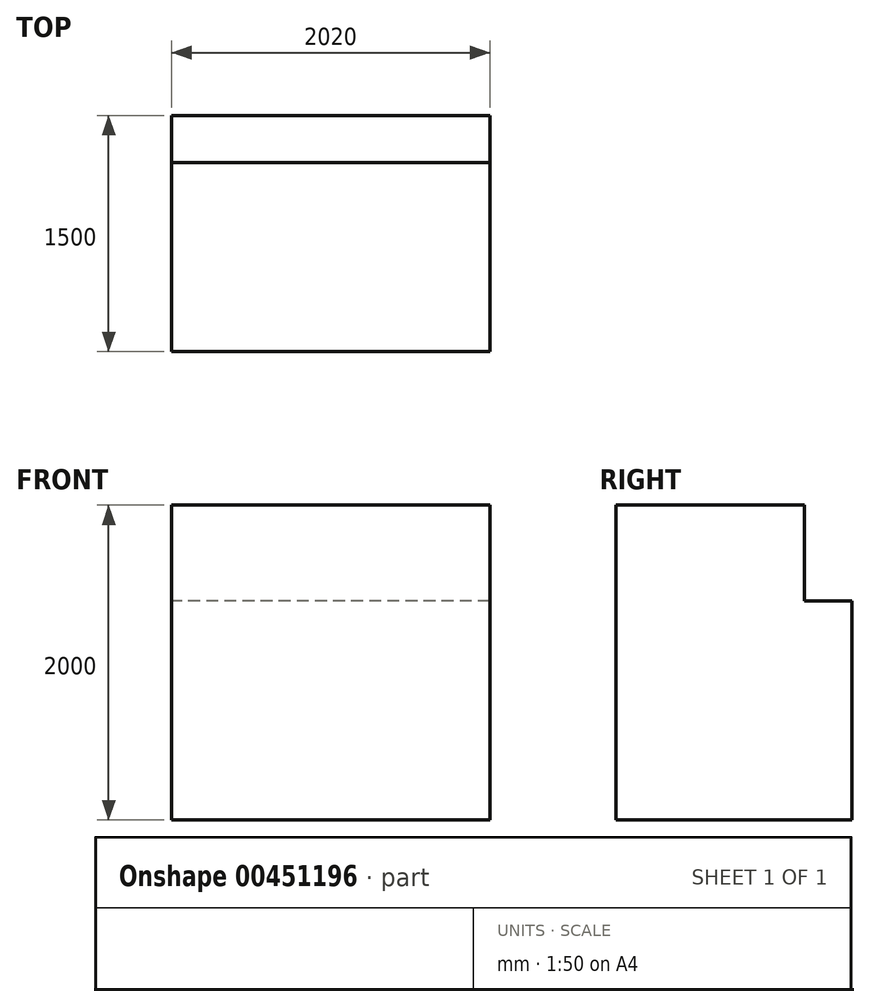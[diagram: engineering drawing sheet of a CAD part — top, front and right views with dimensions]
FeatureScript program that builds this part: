
annotation { "Feature Type Name" : "Feature", "Feature Type Description" : "" }
export const myFeature = defineFeature(function(context is Context, id is Id, definition is map)
    precondition{}
    {
        {
            var Q0;
            Q0=qCreatedBy(makeId("Top.planeOp"),FACE);
            var sketch = newSketch(context, id + "F0", { "sketchPlane" : qUnion([Q0])});
            skLineSegment(sketch, "E0.bottom", {"start": v(1010, -750) * mm, "end": v(-1010, -750) * mm});
            skLineSegment(sketch, "E0.top", {"start": v(1010, 750) * mm, "end": v(-1010, 750) * mm});
            skLineSegment(sketch, "E0.left", {"start": v(1010, -750) * mm, "end": v(1010, 750) * mm});
            skLineSegment(sketch, "E0.right", {"start": v(-1010, -750) * mm, "end": v(-1010, 750) * mm});
            skPoint(sketch, "E0.middle", {"position": v(0, 0) * mm});
            skSolve(sketch);
        }
        {
            var Q0;
            Q0 = qSketchRegion(id + "F0", true);
            extrude(context, id + "F1", {"entities" : qUnion([Q0]), "depth" : 2000 * mm, "offsetDistance" : 25 * mm});
        }
        {
            var Q0;
            Q0=makeQuery(id+"F1.opExtrude","SWEPT_FACE",FACE,{"disambiguationData":[OSD([sQuery(id+"F0.wireOp",EDGE,"E0.right")])]});
            var sketch = newSketch(context, id + "F2", { "sketchPlane" : qUnion([Q0])});
            skLineSegment(sketch, "E1.bottom", {"start": v(-750, 2000) * mm, "end": v(-450, 2000) * mm});
            skLineSegment(sketch, "E1.top", {"start": v(-750, 1392) * mm, "end": v(-450, 1392) * mm});
            skLineSegment(sketch, "E1.left", {"start": v(-750, 2000) * mm, "end": v(-750, 1392) * mm});
            skLineSegment(sketch, "E1.right", {"start": v(-450, 2000) * mm, "end": v(-450, 1392) * mm});
            skLineSegment(sketch, "E2", {"start": v(-447.92, 1360) * mm, "end": v(-840.7, 1360) * mm, "construction": true});
            skSolve(sketch);
        }
        {
            var Q0;
            Q0 = qSketchRegion(id + "F2", true);
            extrude(context, id + "F3", {"entities" : qUnion([Q0]), "operationType" : NewBodyOperationType.REMOVE, "endBound" : BoundingType.THROUGH_ALL, "oppositeDirection" : true, "depth" : 25 * mm, "offsetDistance" : 25 * mm});
        }
    });
